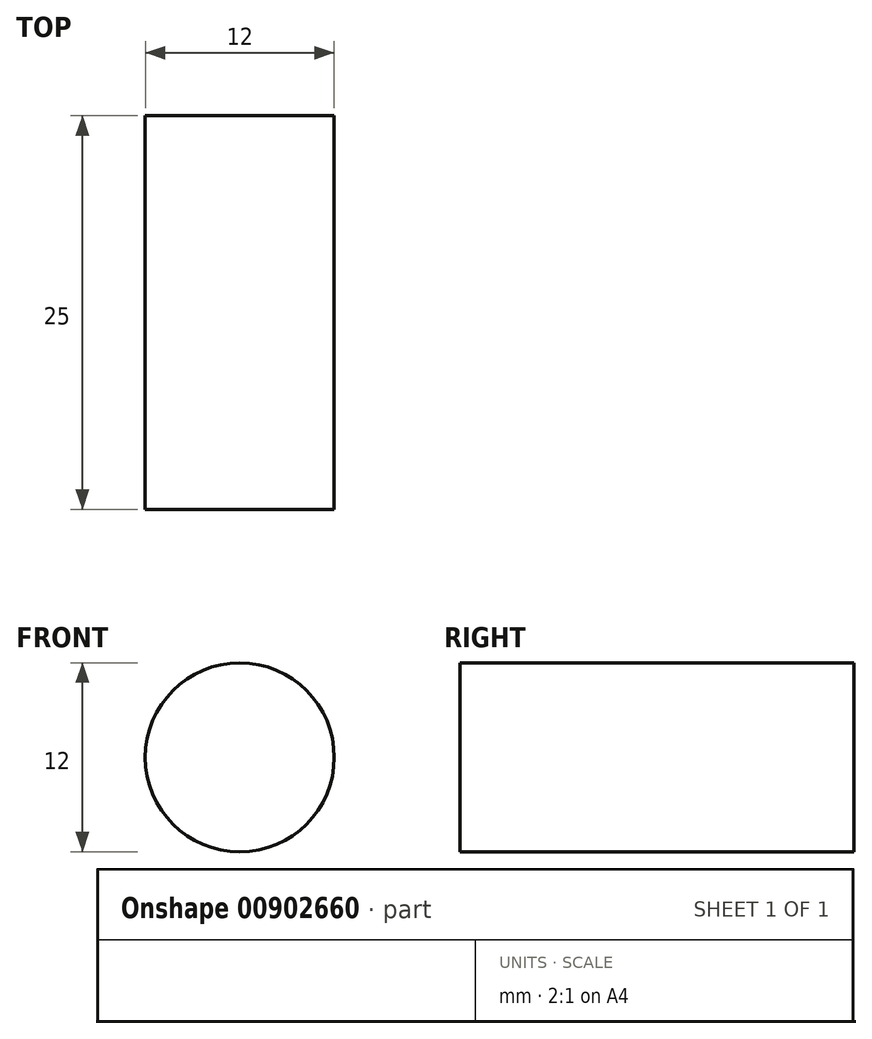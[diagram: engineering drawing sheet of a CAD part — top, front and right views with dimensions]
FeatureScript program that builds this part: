
annotation { "Feature Type Name" : "Feature", "Feature Type Description" : "" }
export const myFeature = defineFeature(function(context is Context, id is Id, definition is map)
    precondition{}
    {
        {
            var Q0;
            Q0=qCreatedBy(makeId("Front.planeOp"),FACE);
            var sketch = newSketch(context, id + "F0", { "sketchPlane" : qUnion([Q0])});
            skCircle(sketch, "E0", {"center": v(-178.58, 58.57) * mm, "radius": 6 * mm});
            skSolve(sketch);
        }
        {
            var Q0;
            Q0=makeQuery(id+"F0.imprint","IMPRINT",FACE,{"disambiguationData":[TD([[makeQuery(id+"F0.imprint","IMPRINT",EDGE,{"derivedFrom":sQuery(id+"F0.wireOp",EDGE,"E0")}),1.0]])]});
            var Q1;
            Q1 = qConstructionFilter(qBodyType(qCreatedBy(id + "F0" ,EDGE), BodyType.WIRE), ConstructionObject.NO);
            extrude(context, id + "F1", {"entities" : qUnion([Q0]), "surfaceEntities" : qUnion([Q1]), "depth" : 25 * mm, "offsetDistance" : 25 * mm});
        }
    });
